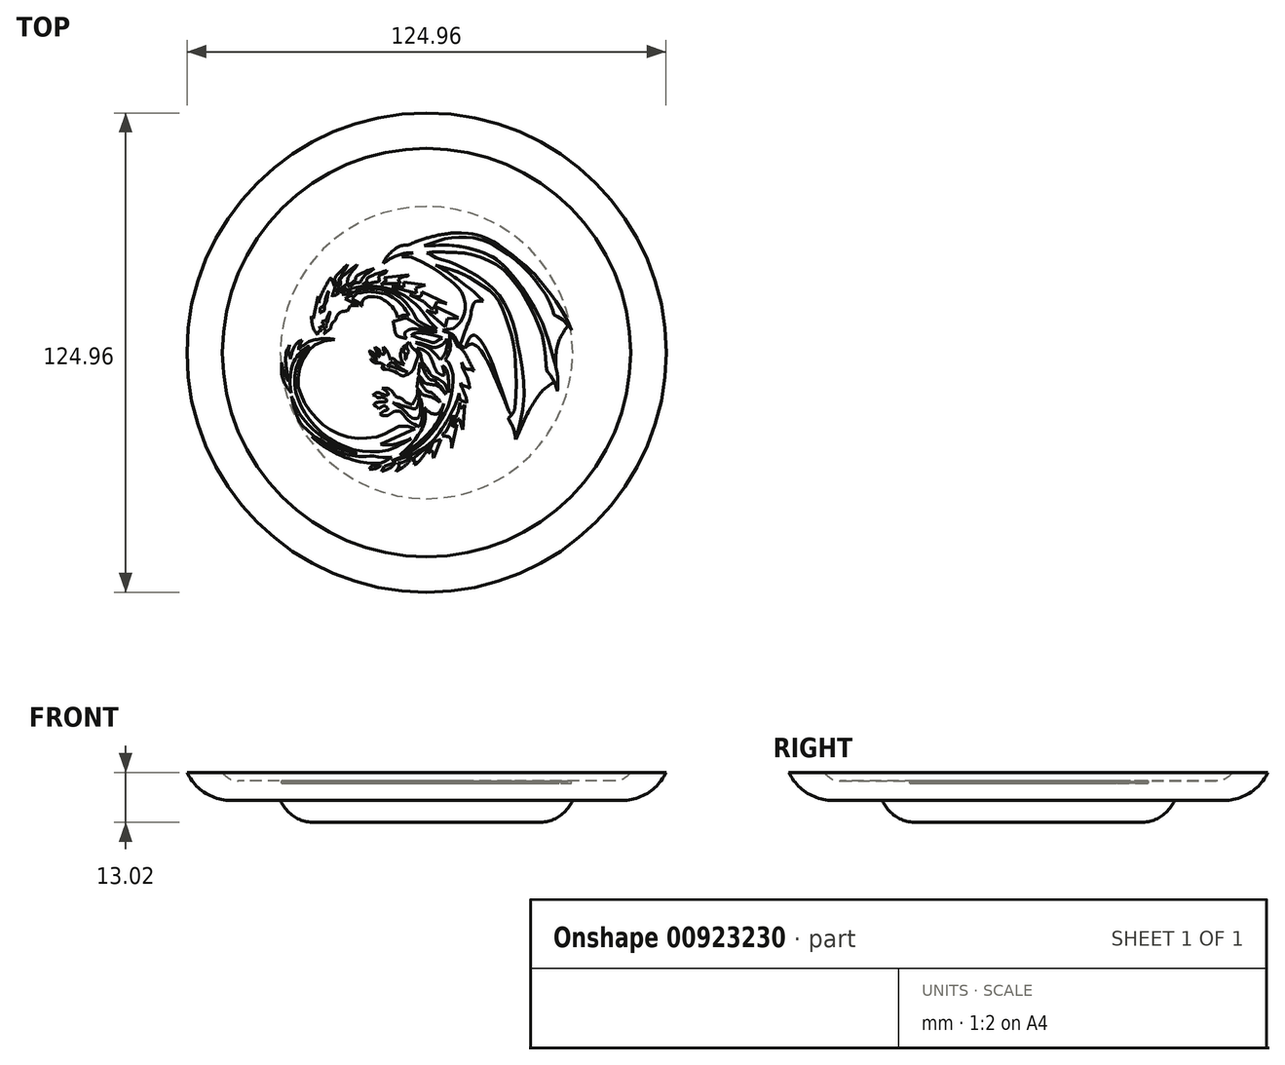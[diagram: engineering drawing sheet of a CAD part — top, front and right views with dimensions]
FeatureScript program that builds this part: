
annotation { "Feature Type Name" : "Feature", "Feature Type Description" : "" }
export const myFeature = defineFeature(function(context is Context, id is Id, definition is map)
    precondition{}
    {
        {
            var Q0;
            Q0=qCreatedBy(makeId("Top.planeOp"),FACE);
            var sketch = newSketch(context, id + "F0", { "sketchPlane" : qUnion([Q0])});
            skCircle(sketch, "E0", {"center": v(0, 0) * mm, "radius": 62.48 * mm});
            skSolve(sketch);
        }
        {
            var Q0;
            Q0=makeQuery(id+"F0.imprint","IMPRINT",FACE,{"disambiguationData":[TD([[makeQuery(id+"F0.imprint","IMPRINT",EDGE,{"derivedFrom":sQuery(id+"F0.wireOp",EDGE,"E0")}),1.0]])]});
            extrude(context, id + "F1", {"entities" : qUnion([Q0]), "depth" : 5.08 * mm, "offsetDistance" : 25.4 * mm});
        }
        {
            var Q0;
            Q0=makeQuery(id+"F1.opExtrude","CAP_FACE",FACE,{"disambiguationData":[OSD([sQuery(id+"F0.wireOp",EDGE,"E0")])],"isStart":false});
            var sketch = newSketch(context, id + "F2", { "sketchPlane" : qUnion([Q0])});
            skCircle(sketch, "E1", {"center": v(0, 0) * mm, "radius": 62.48 * mm});
            skCircle(sketch, "E2", {"center": v(0, 0) * mm, "radius": 53.23 * mm});
            skSolve(sketch);
        }
        {
            var Q0;
            Q0 = qSketchRegion(id + "F2", true);
            extrude(context, id + "F3", {"entities" : qUnion([Q0]), "endBound" : BoundingType.SYMMETRIC, "depth" : 4.44 * mm, "offsetDistance" : 25.4 * mm});
        }
        {
            var Q0;
            Q0=makeQuery(id+"F1.opExtrude","SWEPT_BODY",BODY,{"disambiguationData":[OSD([sQuery(id+"F0.wireOp",EDGE,"E0")])]});
            var Q1;
            Q1=makeQuery(id+"F3.opExtrude","SWEPT_BODY",BODY,{"disambiguationData":[OSD([sQuery(id+"F2.wireOp",EDGE,"E1"),sQuery(id+"F2.wireOp",EDGE,"E2")])]});
            booleanBodies(context, id + "F4", {"operationType" : BooleanOperationType.UNION, "tools" : qUnion([Q0, Q1])});
        }
        {
            var Q0;
            Q0=makeQuery(id+"F1.opExtrude","CAP_FACE",FACE,{"disambiguationData":[OSD([sQuery(id+"F0.wireOp",EDGE,"E0")])],"isStart":false});
            fillet(context, id + "F5", {"entities" : qUnion([Q0]), "radius" : 5.08 * mm, "tangentPropagation" : true, "allowEdgeOverflow" : false});
        }
        {
            var Q0;
            Q0=makeQuery(id+"F1.opExtrude","CAP_FACE",FACE,{"disambiguationData":[OSD([sQuery(id+"F0.wireOp",EDGE,"E0")])],"isStart":true});
            var sketch = newSketch(context, id + "F6", { "sketchPlane" : qUnion([Q0])});
            skCircle(sketch, "E3", {"center": v(0, 0) * mm, "radius": 38.1 * mm});
            skSolve(sketch);
        }
        {
            var Q0;
            Q0 = qSketchRegion(id + "F6", true);
            extrude(context, id + "F7", {"entities" : qUnion([Q0]), "operationType" : NewBodyOperationType.ADD, "depth" : 5.7 * mm, "offsetDistance" : 25.4 * mm});
        }
        {
            var Q0;
            Q0=makeQuery(id+"F7.opExtrude","CAP_EDGE",EDGE,{"disambiguationData":[OSD([sQuery(id+"F6.wireOp",EDGE,"E3")])],"isStart":false});
            fillet(context, id + "F8", {"entities" : qUnion([Q0]), "radius" : 9.52 * mm, "tangentPropagation" : true, "allowEdgeOverflow" : false});
        }
        {
            var Q0;
            Q0=makeQuery(id+"F1.opExtrude","CAP_EDGE",EDGE,{"disambiguationData":[OSD([sQuery(id+"F0.wireOp",EDGE,"E0")])],"isStart":true});
            fillet(context, id + "F9", {"entities" : qUnion([Q0]), "radius" : 12.7 * mm, "tangentPropagation" : true, "allowEdgeOverflow" : false});
        }
        {
            var Q0;
            Q0=makeQuery(id+"F1.opExtrude","CAP_FACE",FACE,{"disambiguationData":[OSD([sQuery(id+"F0.wireOp",EDGE,"E0")])],"isStart":false});
            var sketch = newSketch(context, id + "F10", { "sketchPlane" : qUnion([Q0])});
            skFitSpline(sketch, "E4", {"points": [v(-28.04, 12.93) * mm, v(-27.98, 13.48) * mm, v(-27.55, 14.77) * mm, v(-26.14, 17.67) * mm, v(-25, 19.57) * mm], "startDerivative": vector(0.19, 3.57) * mm, "endDerivative": vector(3.86, 6) * mm});
            skFitSpline(sketch, "E5", {"points": [v(-25, 19.57) * mm, v(-24.5, 18.6) * mm, v(-24.1, 17.53) * mm, v(-23.93, 16.84) * mm, v(-24.33, 15.58) * mm, v(-24.62, 14.6) * mm], "startDerivative": vector(2.5, -4.6) * mm, "endDerivative": vector(-1.17, -4.66) * mm});
            skFitSpline(sketch, "E6", {"points": [v(-24.62, 14.6) * mm, v(-24.27, 14.9) * mm, v(-23.9, 14.9) * mm, v(-23.18, 15.35) * mm, v(-20.91, 16.98) * mm], "startDerivative": vector(1.88, 2.32) * mm, "endDerivative": vector(5.97, 4.22) * mm});
            skLineSegment(sketch, "E7", {"start": v(-20.91, 16.98) * mm, "end": v(-22.03, 15.17) * mm});
            skLineSegment(sketch, "E8", {"start": v(-22.03, 15.17) * mm, "end": v(-19.25, 15.17) * mm});
            skLineSegment(sketch, "E9", {"start": v(-19.25, 15.17) * mm, "end": v(-21.26, 14) * mm});
            skLineSegment(sketch, "E10", {"start": v(-21.26, 14) * mm, "end": v(-17.72, 12.3) * mm});
            skLineSegment(sketch, "E11", {"start": v(-17.72, 12.3) * mm, "end": v(-19.9, 12.3) * mm});
            skLineSegment(sketch, "E12", {"start": v(-19.9, 12.3) * mm, "end": v(-20.63, 10.8) * mm});
            skFitSpline(sketch, "E13", {"points": [v(-23.96, 8.22) * mm, v(-23.64, 8.88) * mm, v(-23.27, 9.66) * mm, v(-22.87, 10.17) * mm, v(-22.3, 10.55) * mm, v(-21.57, 10.78) * mm, v(-20.63, 10.8) * mm], "startDerivative": vector(1.92, 3.92) * mm, "endDerivative": vector(5.3, -0.13) * mm});
            skFitSpline(sketch, "E14", {"points": [v(-23.96, 8.22) * mm, v(-24.48, 7.82) * mm, v(-24.8, 7.27) * mm, v(-25, 6.3) * mm], "startDerivative": vector(-1.8, -1.2) * mm, "endDerivative": vector(-0.42, -2.73) * mm});
            skFitSpline(sketch, "E15", {"points": [v(-25, 6.3) * mm, v(-26.69, 4.89) * mm], "startDerivative": vector(-1.7, -1.4) * mm, "endDerivative": vector(-1.7, -1.4) * mm});
            skFitSpline(sketch, "E16", {"points": [v(-26.69, 4.89) * mm, v(-26.49, 5.38) * mm, v(-26.39, 5.7) * mm, v(-26.47, 5.99) * mm, v(-26.93, 6.3) * mm], "startDerivative": vector(0.76, 1.83) * mm, "endDerivative": vector(-1.93, 0.98) * mm});
            skFitSpline(sketch, "E17", {"points": [v(-26.93, 6.3) * mm, v(-26.45, 6.45) * mm, v(-26.1, 6.7) * mm, v(-26.06, 7.11) * mm, v(-26.27, 7.38) * mm], "startDerivative": vector(1.79, 0.52) * mm, "endDerivative": vector(-1.18, 1.01) * mm});
            skFitSpline(sketch, "E18", {"points": [v(-26.27, 7.38) * mm, v(-25.96, 7.8) * mm, v(-25.68, 8.47) * mm, v(-25.53, 8.96) * mm, v(-25.34, 9.66) * mm, v(-25.25, 10.1) * mm, v(-25.2, 10.57) * mm, v(-25.4, 10.34) * mm, v(-25.7, 9.62) * mm, v(-25.98, 8.75) * mm, v(-25.98, 8.6) * mm], "startDerivative": vector(3.31, 3.75) * mm, "endDerivative": vector(0.36, -2.21) * mm});
            skFitSpline(sketch, "E19", {"points": [v(-25.98, 8.6) * mm, v(-26.66, 8.26) * mm, v(-27.38, 8.02) * mm], "startDerivative": vector(-1.34, -0.73) * mm, "endDerivative": vector(-1.45, -0.45) * mm});
            skFitSpline(sketch, "E20", {"points": [v(-27.87, 6.76) * mm, v(-27.52, 6.73) * mm, v(-27.17, 6.84) * mm, v(-26.63, 7.18) * mm], "startDerivative": vector(1.2, -0.18) * mm, "endDerivative": vector(1.42, 0.96) * mm});
            skFitSpline(sketch, "E21", {"points": [v(-27.38, 8.02) * mm, v(-26.63, 7.18) * mm], "startDerivative": vector(0.75, -0.84) * mm, "endDerivative": vector(0.75, -0.84) * mm});
            skFitSpline(sketch, "E22", {"points": [v(-27.87, 6.76) * mm, v(-27.82, 6.47) * mm, v(-27.6, 6.07) * mm, v(-27.24, 5.75) * mm], "startDerivative": vector(0.1, -0.97) * mm, "endDerivative": vector(1.1, -0.77) * mm});
            skFitSpline(sketch, "E23", {"points": [v(-28.4, 4.67) * mm, v(-28.34, 4.98) * mm, v(-28.26, 5.28) * mm, v(-28, 5.63) * mm, v(-27.46, 5.74) * mm, v(-27.24, 5.75) * mm], "startDerivative": vector(0.2, 1.61) * mm, "endDerivative": vector(1.17, 0.05) * mm});
            skFitSpline(sketch, "E24", {"points": [v(-28.4, 4.67) * mm, v(-28.6, 4.85) * mm, v(-28.86, 5.17) * mm, v(-29.12, 5.54) * mm, v(-29.4, 6.03) * mm, v(-29.58, 6.52) * mm, v(-29.7, 6.9) * mm, v(-29.8, 7.36) * mm, v(-29.89, 7.96) * mm, v(-29.96, 8.44) * mm, v(-30.02, 9.03) * mm, v(-30.1, 9.47) * mm], "startDerivative": vector(-2.77, 2.4) * mm, "endDerivative": vector(-0.92, 4.7) * mm});
            skLineSegment(sketch, "E25", {"start": v(-30.1, 9.47) * mm, "end": v(-29.5, 8.8) * mm});
            skLineSegment(sketch, "E26", {"start": v(-29.5, 8.8) * mm, "end": v(-28.25, 14.66) * mm});
            skLineSegment(sketch, "E27", {"start": v(-28.25, 14.66) * mm, "end": v(-28.04, 12.93) * mm});
            skFitSpline(sketch, "E28", {"points": [v(-27.7, 11.73) * mm, v(-27.7, 10.38) * mm], "startDerivative": vector(0.01, -1.36) * mm, "endDerivative": vector(0.01, -1.36) * mm});
            skFitSpline(sketch, "E29", {"points": [v(-27.7, 11.73) * mm, v(-27.38, 11.83) * mm, v(-27.1, 12.04) * mm, v(-26.88, 12.27) * mm, v(-26.57, 13) * mm, v(-25.8, 15.63) * mm, v(-25.7, 15.87) * mm, v(-25.64, 15.94) * mm, v(-25.62, 15.76) * mm, v(-26.3, 12.85) * mm, v(-26.63, 12.03) * mm, v(-26.64, 11.17) * mm], "startDerivative": vector(5.23, 1.12) * mm, "endDerivative": vector(0.62, -9.26) * mm});
            skFitSpline(sketch, "E30", {"points": [v(-27.7, 10.38) * mm, v(-27.52, 10.55) * mm, v(-27.27, 10.67) * mm, v(-26.95, 10.73) * mm, v(-26.75, 10.88) * mm, v(-26.64, 11.17) * mm], "startDerivative": vector(0.88, 1.01) * mm, "endDerivative": vector(0.41, 1.5) * mm});
            skFitSpline(sketch, "E31", {"points": [v(-8.75, 8.21) * mm, v(-8.37, 8.23) * mm, v(-7.9, 8.3) * mm, v(-7.35, 8.47) * mm, v(-6.92, 8.66) * mm, v(-6.56, 8.77) * mm, v(-6.14, 8.89) * mm, v(-5.65, 8.94) * mm, v(-5.17, 8.94) * mm, v(-4.69, 8.76) * mm, v(-4.16, 8.44) * mm, v(-3.7, 8.16) * mm, v(-3.22, 7.83) * mm, v(-2.67, 7.43) * mm, v(-2.24, 7.19) * mm, v(-1.71, 6.89) * mm, v(-1.07, 6.57) * mm, v(-0.5, 6.34) * mm, v(0, 6.16) * mm, v(0.75, 5.96) * mm, v(1.44, 5.83) * mm, v(1.97, 5.78) * mm], "startDerivative": vector(9.36, 0.14) * mm, "endDerivative": vector(10.96, -0.78) * mm});
            skFitSpline(sketch, "E32", {"points": [v(-8.75, 8.21) * mm, v(-8.66, 7.74) * mm, v(-8.54, 7.27) * mm, v(-8.4, 6.67) * mm, v(-8.3, 6.08) * mm, v(-8.21, 5.56) * mm, v(-8.12, 5.16) * mm, v(-8, 4.8) * mm, v(-7.8, 4.5) * mm, v(-7.48, 4.27) * mm, v(-7.03, 4.09) * mm, v(-6.6, 3.96) * mm, v(-6.25, 3.87) * mm, v(-5.75, 3.75) * mm, v(-5.15, 3.68) * mm], "startDerivative": vector(1.31, -6.58) * mm, "endDerivative": vector(7.6, -0.57) * mm});
            skFitSpline(sketch, "E33", {"points": [v(1.97, 5.78) * mm, v(2.69, 5.41) * mm], "startDerivative": vector(0.71, -0.37) * mm, "endDerivative": vector(0.71, -0.37) * mm});
            skFitSpline(sketch, "E34", {"points": [v(2.69, 5.41) * mm, v(2.12, 5.41) * mm, v(1.67, 5.41) * mm, v(0.66, 5.52) * mm, v(0, 5.6) * mm, v(-0.74, 5.78) * mm, v(-1.43, 5.92) * mm, v(-2.13, 6.07) * mm, v(-2.9, 6.16) * mm, v(-3.84, 6.16) * mm, v(-4.63, 5.95) * mm, v(-5.22, 5.62) * mm, v(-5.56, 5.25) * mm, v(-5.7, 4.77) * mm, v(-5.55, 4.24) * mm, v(-5.15, 3.68) * mm], "startDerivative": vector(-9.85, 0.1) * mm, "endDerivative": vector(6.65, -8.24) * mm});
            skFitSpline(sketch, "E35", {"points": [v(-16.78, 12.16) * mm, v(-16.82, 12.74) * mm, v(-16.7, 13.46) * mm, v(-16.13, 14.1) * mm, v(-15.32, 14.47) * mm, v(-14.33, 14.58) * mm, v(-12.82, 14.44) * mm, v(-11.38, 13.89) * mm, v(-10.26, 13.15) * mm, v(-8.8, 11.77) * mm, v(-7.83, 10.11) * mm, v(-7.52, 9.13) * mm], "startDerivative": vector(-0.9, 8.75) * mm, "endDerivative": vector(2.8, -10.83) * mm});
            skFitSpline(sketch, "E36", {"points": [v(-16.78, 12.16) * mm, v(-17.1, 12.3) * mm, v(-17.33, 12.69) * mm, v(-17.6, 12.98) * mm, v(-18.03, 13.27) * mm, v(-18.72, 13.59) * mm, v(-19.13, 13.85) * mm, v(-19.36, 14.17) * mm], "startDerivative": vector(-2.84, 0.74) * mm, "endDerivative": vector(-1.6, 2.6) * mm});
            skFitSpline(sketch, "E37", {"points": [v(-19.36, 14.17) * mm, v(-18, 15.55) * mm], "startDerivative": vector(1.37, 1.38) * mm, "endDerivative": vector(1.37, 1.38) * mm});
            skFitSpline(sketch, "E38", {"points": [v(-18, 15.55) * mm, v(-17.5, 15.55) * mm, v(-16.78, 15.7) * mm, v(-16.13, 15.8) * mm, v(-15.35, 15.89) * mm, v(-14.44, 15.87) * mm, v(-13.17, 15.77) * mm, v(-11.9, 15.55) * mm, v(-10.25, 15.09) * mm, v(-8.98, 14.47) * mm, v(-7.38, 13.33) * mm, v(-6.44, 12.45) * mm, v(-5.38, 11.06) * mm, v(-4.59, 9.63) * mm], "startDerivative": vector(9.45, -0.58) * mm, "endDerivative": vector(8.06, -15.64) * mm});
            skFitSpline(sketch, "E39", {"points": [v(-7.52, 9.13) * mm, v(-7.08, 9.34) * mm, v(-6.6, 9.58) * mm, v(-5.82, 9.75) * mm, v(-4.59, 9.63) * mm], "startDerivative": vector(2.07, 1.08) * mm, "endDerivative": vector(4.13, -0.76) * mm});
            skFitSpline(sketch, "E40", {"points": [v(-20.93, 15.76) * mm, v(-20.63, 16.11) * mm, v(-19.99, 16.5) * mm, v(-19.04, 16.83) * mm, v(-17.63, 17.11) * mm, v(-15.8, 17.3) * mm, v(-13.72, 17.3) * mm, v(-12.44, 17.16) * mm, v(-11.33, 17) * mm, v(-9.91, 16.68) * mm, v(-8.5, 16.23) * mm, v(-7, 15.55) * mm, v(-5.54, 14.68) * mm, v(-4.57, 14.02) * mm, v(-3.54, 13.25) * mm, v(-2.5, 12.23) * mm, v(-1.52, 11.2) * mm, v(-0.68, 10.23) * mm, v(0.3, 8.93) * mm, v(0.9, 8.06) * mm, v(2.29, 6.68) * mm, v(2.77, 6.22) * mm], "startDerivative": vector(9.28, 12.83) * mm, "endDerivative": vector(11.69, -11.13) * mm});
            skFitSpline(sketch, "E41", {"points": [v(2.77, 6.22) * mm, v(1.24, 6.52) * mm, v(-0.86, 7.43) * mm, v(-2.01, 8.21) * mm, v(-2.67, 8.79) * mm, v(-3.1, 9.68) * mm, v(-3.67, 10.76) * mm, v(-4.37, 11.75) * mm, v(-5.48, 13.1) * mm, v(-6.98, 14.44) * mm, v(-8.75, 15.45) * mm, v(-11.33, 16.33) * mm, v(-13.54, 16.68) * mm, v(-15.96, 16.68) * mm, v(-18.37, 16.08) * mm, v(-18.84, 15.66) * mm], "startDerivative": vector(-22.2, 3.08) * mm, "endDerivative": vector(-1.37, -8.56) * mm});
            skFitSpline(sketch, "E42", {"points": [v(-20.93, 15.76) * mm, v(-18.84, 15.66) * mm], "startDerivative": vector(2.1, -0.1) * mm, "endDerivative": vector(2.1, -0.1) * mm});
            skFitSpline(sketch, "E43", {"points": [v(-3.95, 4.44) * mm, v(-3.72, 4.65) * mm, v(-3.26, 4.95) * mm, v(-2.39, 5.16) * mm, v(-1.16, 5.08) * mm, v(2.74, 4.34) * mm, v(4.1, 3.8) * mm], "startDerivative": vector(2.53, 2.3) * mm, "endDerivative": vector(5.84, -2.9) * mm});
            skFitSpline(sketch, "E44", {"points": [v(4.1, 3.8) * mm, v(3.23, 3.31) * mm, v(2.56, 2.8) * mm, v(1.94, 2.6) * mm, v(0.3, 2.95) * mm, v(-3.95, 4.44) * mm], "startDerivative": vector(-5.6, -2.77) * mm, "endDerivative": vector(-13.5, 4.87) * mm});
            skFitSpline(sketch, "E45", {"points": [v(5.26, 3.68) * mm, v(5.33, 3) * mm, v(5.38, 2.06) * mm, v(5.16, 0.74) * mm, v(4.49, -0.78) * mm, v(4.04, -1.43) * mm, v(3.64, -1.88) * mm], "startDerivative": vector(0.54, -4.67) * mm, "endDerivative": vector(-2.9, -3.43) * mm});
            skFitSpline(sketch, "E46", {"points": [v(-2.87, 2.6) * mm, v(-1.8, 2.5) * mm, v(-0.65, 2.16) * mm, v(0.37, 1.73) * mm, v(1.37, 1.46) * mm, v(2.44, 1.39) * mm, v(3.71, 1.8) * mm, v(4.69, 2.6) * mm, v(5.26, 3.68) * mm], "startDerivative": vector(8.83, -0.4) * mm, "endDerivative": vector(3.84, 8.84) * mm});
            skFitSpline(sketch, "E47", {"points": [v(-2.5, 1.28) * mm, v(-1.2, 0.82) * mm, v(0.33, -0.2) * mm, v(1.03, -1.2) * mm, v(1.67, -2.59) * mm, v(2.37, -4.54) * mm, v(3.36, -5.62) * mm, v(4.44, -5.9) * mm, v(4.79, -5.67) * mm], "startDerivative": vector(9.7, -2.95) * mm, "endDerivative": vector(4, 4.29) * mm});
            skFitSpline(sketch, "E48", {"points": [v(-2.87, 2.6) * mm, v(-1.76, 2.16) * mm, v(-0.48, 1.7) * mm, v(0.83, 1.02) * mm, v(1.93, 0) * mm, v(3.64, -1.88) * mm], "startDerivative": vector(6.15, -2.7) * mm, "endDerivative": vector(6.76, -8.1) * mm});
            skFitSpline(sketch, "E49", {"points": [v(4.79, -5.67) * mm, v(4.1, -3.41) * mm], "startDerivative": vector(-0.7, 2.26) * mm, "endDerivative": vector(-0.7, 2.26) * mm});
            skFitSpline(sketch, "E50", {"points": [v(5.77, -10.5) * mm, v(5.32, -9.46) * mm, v(5.04, -8.67) * mm, v(4.75, -8.15) * mm, v(4.18, -7.63) * mm, v(2.9, -6.85) * mm, v(1.65, -6.18) * mm, v(1.13, -5.73) * mm, v(0.44, -4.71) * mm, v(0, -3.9) * mm, v(-0.53, -3.15) * mm, v(-1.03, -2.58) * mm, v(-1.27, -1.9) * mm, v(-1.46, -0.82) * mm, v(-1.58, -0.3) * mm, v(-2, 0.48) * mm, v(-2.5, 1.28) * mm], "startDerivative": vector(-6.97, 15.32) * mm, "endDerivative": vector(-7.53, 12.46) * mm});
            skFitSpline(sketch, "E51", {"points": [v(4.1, -3.41) * mm, v(4.59, -3.67) * mm, v(5.13, -4.31) * mm, v(5.49, -5.21) * mm, v(5.68, -6.52) * mm, v(5.77, -10.5) * mm], "startDerivative": vector(3.88, -1.58) * mm, "endDerivative": vector(0.12, -13.13) * mm});
            skFitSpline(sketch, "E52", {"points": [v(-1.67, -2.53) * mm, v(-2.05, -5.8) * mm], "startDerivative": vector(-0.39, -3.27) * mm, "endDerivative": vector(-0.39, -3.27) * mm});
            skFitSpline(sketch, "E53", {"points": [v(-1.67, -2.53) * mm, v(-0.96, -4.03) * mm, v(-0.37, -5.41) * mm, v(0.33, -6.48) * mm, v(1.15, -7.1) * mm, v(1.94, -7.25) * mm, v(2.78, -7.89) * mm, v(3.8, -8.91) * mm, v(4.96, -10.5) * mm], "startDerivative": vector(5.26, -10.7) * mm, "endDerivative": vector(7.48, -11.1) * mm});
            skFitSpline(sketch, "E54", {"points": [v(4.96, -10.5) * mm, v(4.96, -10.86) * mm], "startDerivative": vector(0, -0.36) * mm, "endDerivative": vector(0, -0.36) * mm});
            skFitSpline(sketch, "E55", {"points": [v(4.96, -10.86) * mm, v(4.7, -10.5) * mm, v(4.1, -9.73) * mm, v(3.41, -9.04) * mm, v(2.47, -8.54) * mm, v(1.1, -8.31) * mm, v(0.2, -8.16) * mm, v(-0.46, -7.85) * mm, v(-1.27, -6.8) * mm, v(-2.05, -5.8) * mm], "startDerivative": vector(-3.06, 4.38) * mm, "endDerivative": vector(-6.25, 7.43) * mm});
            skFitSpline(sketch, "E56", {"points": [v(-2.12, -6.24) * mm, v(-2.48, -9.1) * mm], "startDerivative": vector(-0.28, -2.87) * mm, "endDerivative": vector(-0.28, -2.87) * mm});
            skFitSpline(sketch, "E57", {"points": [v(3.5, -12.63) * mm, v(3.5, -13) * mm], "startDerivative": vector(-0.02, -0.37) * mm, "endDerivative": vector(-0.02, -0.37) * mm});
            skFitSpline(sketch, "E58", {"points": [v(-2.48, -9.1) * mm, v(-1.34, -10.62) * mm, v(-1, -10.96) * mm, v(0, -11.29) * mm, v(1.64, -11.76) * mm, v(3.16, -12.67) * mm, v(3.5, -13) * mm], "startDerivative": vector(5.4, -8.78) * mm, "endDerivative": vector(2.33, -2.73) * mm});
            skFitSpline(sketch, "E59", {"points": [v(-2.12, -6.24) * mm, v(-1.33, -8.01) * mm, v(-0.96, -8.78) * mm, v(-0.5, -9.5) * mm, v(0, -10.04) * mm, v(0.7, -10.29) * mm, v(1.42, -10.56) * mm, v(2.38, -11.43) * mm, v(3.5, -12.63) * mm], "startDerivative": vector(5.15, -11.65) * mm, "endDerivative": vector(7.3, -7.88) * mm});
            skFitSpline(sketch, "E60", {"points": [v(-0.54, -14.34) * mm, v(0, -14.94) * mm, v(0.7, -15.52) * mm, v(1.85, -16.02) * mm, v(2.86, -15.87) * mm, v(3.82, -14.87) * mm, v(4.47, -13.3) * mm], "startDerivative": vector(3.55, -4.47) * mm, "endDerivative": vector(2.7, 8.16) * mm});
            skFitSpline(sketch, "E61", {"points": [v(-6.96, -26.68) * mm, v(-5.37, -25.78) * mm, v(-2.57, -23.93) * mm, v(0, -21.6) * mm, v(1.91, -19.35) * mm, v(3.5, -16.56) * mm, v(4.47, -13.3) * mm], "startDerivative": vector(11.38, 6.23) * mm, "endDerivative": vector(4.5, 18.8) * mm});
            skFitSpline(sketch, "E62", {"points": [v(-0.54, -14.34) * mm, v(-0.28, -15.56) * mm, v(-0.28, -16.48) * mm, v(-0.54, -18.3) * mm, v(-1.8, -20.95) * mm, v(-3.86, -23.76) * mm, v(-6.96, -26.68) * mm], "startDerivative": vector(2.65, -10.49) * mm, "endDerivative": vector(-14.5, -12.62) * mm});
            skFitSpline(sketch, "E63", {"points": [v(-4.47, 2.76) * mm, v(-5.14, 2.27) * mm], "startDerivative": vector(-0.67, -0.49) * mm, "endDerivative": vector(-0.67, -0.49) * mm});
            skFitSpline(sketch, "E64", {"points": [v(-4.47, 2.76) * mm, v(-4.27, 2.17) * mm, v(-3.7, 1.27) * mm, v(-2.88, 0.52) * mm, v(-2.37, 0) * mm, v(-2.17, -0.5) * mm, v(-2.31, -1.4) * mm, v(-2.92, -3.08) * mm, v(-3.64, -4.8) * mm, v(-4.47, -5.5) * mm, v(-5.37, -5.9) * mm, v(-5.94, -6.07) * mm, v(-6.47, -6.05) * mm, v(-7.34, -5.52) * mm, v(-8.03, -5.08) * mm, v(-8.85, -4.71) * mm, v(-9.8, -4.43) * mm, v(-10.68, -4.36) * mm, v(-11.31, -4.36) * mm, v(-11.54, -4.18) * mm, v(-11.7, -3.9) * mm, v(-11.45, -3.63) * mm, v(-10.9, -3.45) * mm], "startDerivative": vector(3.99, -13.9) * mm, "endDerivative": vector(14.88, 3.67) * mm});
            skFitSpline(sketch, "E65", {"points": [v(-5.14, 2.27) * mm, v(-5.14, 1.91) * mm, v(-5.14, 1.14) * mm, v(-4.73, 0.35) * mm, v(-4.75, 0) * mm, v(-5.04, -0.44) * mm, v(-5.39, -1.8) * mm], "startDerivative": vector(0.18, -3.36) * mm, "endDerivative": vector(-1.16, -6.53) * mm});
            skFitSpline(sketch, "E66", {"points": [v(-5.39, -1.8) * mm, v(-5.54, -1.8) * mm, v(-5.57, -1.32) * mm, v(-5.54, -0.37) * mm, v(-5.71, -0.11) * mm, v(-5.93, 0.16) * mm, v(-5.96, 0.58) * mm, v(-5.56, 1.9) * mm], "startDerivative": vector(-2.31, -0.59) * mm, "endDerivative": vector(2.23, 6.4) * mm});
            skFitSpline(sketch, "E67", {"points": [v(-5.56, 1.9) * mm, v(-5.97, 1.54) * mm, v(-6.65, 0.25) * mm, v(-6.78, -0.89) * mm, v(-6.53, -1.92) * mm, v(-5.79, -3.15) * mm], "startDerivative": vector(-2.8, -1.88) * mm, "endDerivative": vector(3.87, -5.33) * mm});
            skFitSpline(sketch, "E68", {"points": [v(-9.4, -1.99) * mm, v(-9.27, -1.76) * mm, v(-9.04, -1.54) * mm, v(-8.65, -1.62) * mm, v(-8.25, -1.95) * mm, v(-7.5, -2.5) * mm, v(-6.9, -2.84) * mm, v(-6.07, -3.1) * mm, v(-5.79, -3.15) * mm], "startDerivative": vector(1.29, 2.48) * mm, "endDerivative": vector(2.56, -0.43) * mm});
            skFitSpline(sketch, "E69", {"points": [v(-11.26, 1.44) * mm, v(-10.42, 0.54) * mm, v(-9.92, -0.37) * mm, v(-9.4, -1.99) * mm], "startDerivative": vector(2.85, -2.75) * mm, "endDerivative": vector(1.34, -4.6) * mm});
            skFitSpline(sketch, "E70", {"points": [v(-11.26, 1.44) * mm, v(-11.26, 0.61) * mm, v(-10.99, 0) * mm, v(-10.99, -0.4) * mm, v(-11.26, -0.46) * mm, v(-11.75, -0.34) * mm, v(-12.12, 0) * mm, v(-12.26, 0.66) * mm], "startDerivative": vector(-0.57, -4.87) * mm, "endDerivative": vector(0.04, 4.39) * mm});
            skFitSpline(sketch, "E71", {"points": [v(-12.26, 0.66) * mm, v(-13.35, 1.47) * mm], "startDerivative": vector(-1.1, 0.8) * mm, "endDerivative": vector(-1.1, 0.8) * mm});
            skFitSpline(sketch, "E72", {"points": [v(-13.35, 1.47) * mm, v(-13.35, 0.99) * mm, v(-13.2, 0.45) * mm, v(-12.75, -0.32) * mm, v(-12.4, -0.69) * mm, v(-12.26, -0.94) * mm, v(-12.46, -1.12) * mm, v(-12.8, -1.1) * mm, v(-13.23, -0.77) * mm, v(-13.7, -0.2) * mm, v(-13.88, 0) * mm], "startDerivative": vector(-0.26, -4.77) * mm, "endDerivative": vector(-1.9, 2.34) * mm});
            skFitSpline(sketch, "E73", {"points": [v(-14.79, 0.56) * mm, v(-14.47, 0.26) * mm, v(-14.24, 0.1) * mm, v(-13.88, 0) * mm], "startDerivative": vector(0.89, -0.88) * mm, "endDerivative": vector(1.14, -0.2) * mm});
            skFitSpline(sketch, "E74", {"points": [v(-14.79, 0.56) * mm, v(-14.79, 0.16) * mm, v(-14.57, -0.42) * mm, v(-13.75, -1.13) * mm, v(-13.22, -1.47) * mm, v(-12.99, -1.8) * mm, v(-12.95, -2) * mm, v(-13.26, -2.08) * mm, v(-13.94, -1.92) * mm, v(-14.56, -1.66) * mm], "startDerivative": vector(-0.24, -4.02) * mm, "endDerivative": vector(-4.83, 2.1) * mm});
            skFitSpline(sketch, "E75", {"points": [v(-14.56, -1.66) * mm, v(-14.36, -2.04) * mm, v(-13.83, -2.5) * mm, v(-13.35, -2.72) * mm, v(-12.66, -2.72) * mm, v(-12.12, -2.72) * mm, v(-11.56, -2.96) * mm, v(-11.13, -3.27) * mm, v(-10.9, -3.45) * mm], "startDerivative": vector(1.32, -3.34) * mm, "endDerivative": vector(2.27, -1.83) * mm});
            skFitSpline(sketch, "E76", {"points": [v(-9.13, -2.6) * mm, v(-8.81, -2.6) * mm, v(-8.3, -2.94) * mm, v(-7.34, -3.62) * mm, v(-5.7, -4.76) * mm, v(-4.95, -5.12) * mm], "startDerivative": vector(2.63, 0.3) * mm, "endDerivative": vector(3.48, -1.42) * mm});
            skFitSpline(sketch, "E77", {"points": [v(-10.4, -3.47) * mm, v(-9.94, -3.22) * mm, v(-9.42, -2.7) * mm, v(-9.13, -2.6) * mm], "startDerivative": vector(1.33, 0.53) * mm, "endDerivative": vector(1.04, 0.24) * mm});
            skFitSpline(sketch, "E78", {"points": [v(-10.4, -3.47) * mm, v(-8.9, -3.71) * mm, v(-6.79, -4.47) * mm, v(-4.95, -5.12) * mm], "startDerivative": vector(4.78, -0.5) * mm, "endDerivative": vector(5.27, -1.78) * mm});
            skFitSpline(sketch, "E79", {"points": [v(-2.36, -9.73) * mm, v(-2.32, -10.62) * mm, v(-2.51, -11.42) * mm, v(-3.24, -12.76) * mm, v(-3.71, -13.58) * mm], "startDerivative": vector(0.34, -4.07) * mm, "endDerivative": vector(-1.8, -3.12) * mm});
            skFitSpline(sketch, "E80", {"points": [v(-3.71, -13.58) * mm, v(-5.64, -12.87) * mm], "startDerivative": vector(-1.93, 0.7) * mm, "endDerivative": vector(-1.93, 0.7) * mm});
            skFitSpline(sketch, "E81", {"points": [v(-5.64, -12.87) * mm, v(-6.08, -12.32) * mm, v(-6.42, -12.03) * mm, v(-7.1, -11.75) * mm, v(-7.63, -11.65) * mm, v(-8.16, -11.36) * mm, v(-8.6, -10.62) * mm, v(-9.82, -9.51) * mm, v(-11.56, -9.26) * mm], "startDerivative": vector(-4.07, 5.36) * mm, "endDerivative": vector(-10.12, 0) * mm});
            skFitSpline(sketch, "E82", {"points": [v(-11.56, -9.26) * mm, v(-10.64, -9.95) * mm, v(-10.02, -10.62) * mm, v(-10, -10.96) * mm, v(-10.4, -11.15) * mm, v(-11.1, -11) * mm, v(-11.94, -10.62) * mm, v(-12.8, -10.41) * mm, v(-13.98, -11.07) * mm], "startDerivative": vector(6.26, -4.35) * mm, "endDerivative": vector(-7.5, -5.67) * mm});
            skFitSpline(sketch, "E83", {"points": [v(-13.98, -11.07) * mm, v(-13.24, -11.33) * mm, v(-12.78, -11.85) * mm], "startDerivative": vector(1.56, -0.34) * mm, "endDerivative": vector(0.84, -1.22) * mm});
            skFitSpline(sketch, "E84", {"points": [v(-12.78, -11.85) * mm, v(-12.12, -11.67) * mm, v(-10.9, -11.85) * mm, v(-10.4, -12.35) * mm, v(-10.68, -12.87) * mm, v(-12.12, -12.87) * mm, v(-13.23, -13.17) * mm, v(-13.83, -13.75) * mm], "startDerivative": vector(4.76, 1.83) * mm, "endDerivative": vector(-3.96, -4.67) * mm});
            skFitSpline(sketch, "E85", {"points": [v(-13.83, -13.75) * mm, v(-13.17, -13.99) * mm, v(-12.55, -14.63) * mm], "startDerivative": vector(1.46, -0.33) * mm, "endDerivative": vector(1.1, -1.4) * mm});
            skFitSpline(sketch, "E86", {"points": [v(-12.55, -14.63) * mm, v(-11.56, -14.12) * mm, v(-10.9, -13.9) * mm, v(-10.4, -14.26) * mm, v(-10.04, -14.63) * mm], "startDerivative": vector(3.3, 1.66) * mm, "endDerivative": vector(1.57, -1.66) * mm});
            skFitSpline(sketch, "E87", {"points": [v(-10.04, -14.63) * mm, v(-10.25, -14.94) * mm, v(-11.26, -15.25) * mm], "startDerivative": vector(-0.38, -0.9) * mm, "endDerivative": vector(-1.94, -0.4) * mm});
            skFitSpline(sketch, "E88", {"points": [v(-11.26, -15.25) * mm, v(-12.12, -16.08) * mm], "startDerivative": vector(-0.86, -0.84) * mm, "endDerivative": vector(-0.86, -0.84) * mm});
            skFitSpline(sketch, "E89", {"points": [v(-12.12, -16.08) * mm, v(-11.26, -16.44) * mm, v(-10.4, -16.46) * mm, v(-9.5, -16.08) * mm, v(-8.59, -15.48) * mm, v(-7.6, -15.25) * mm, v(-6.67, -15.53) * mm, v(-5.64, -16.8) * mm, v(-4.08, -18.2) * mm, v(-1.8, -19.38) * mm], "startDerivative": vector(9, -4.54) * mm, "endDerivative": vector(15.3, -6.96) * mm});
            skFitSpline(sketch, "E90", {"points": [v(-1.55, -12.02) * mm, v(-1.34, -12.87) * mm, v(-1.15, -14.13) * mm, v(-1.06, -15.6) * mm, v(-1.08, -16.8) * mm, v(-1.8, -19.38) * mm], "startDerivative": vector(1.4, -5.21) * mm, "endDerivative": vector(-3.48, -10.46) * mm});
            skFitSpline(sketch, "E91", {"points": [v(-1.55, -12.02) * mm, v(-1.55, -13.58) * mm, v(-1.55, -14.63) * mm, v(-1.8, -16.38) * mm, v(-2.42, -17.13) * mm, v(-3.57, -17.14) * mm, v(-4.95, -16.08) * mm, v(-5.86, -15.07) * mm, v(-7, -14.22) * mm, v(-8.69, -13.15) * mm, v(-8.8, -13.05) * mm], "startDerivative": vector(-0.08, -15) * mm, "endDerivative": vector(-1.7, 2.88) * mm});
            skFitSpline(sketch, "E92", {"points": [v(-8.8, -13.05) * mm, v(-5.64, -14.03) * mm, v(-3.5, -14.63) * mm, v(-2.78, -14.63) * mm, v(-2.1, -13.05) * mm, v(-1.8, -11.07) * mm], "startDerivative": vector(12.22, -4.07) * mm, "endDerivative": vector(0.05, 9.27) * mm});
            skFitSpline(sketch, "E93", {"points": [v(-1.8, -11.07) * mm, v(-2.36, -9.73) * mm], "startDerivative": vector(-0.55, 1.34) * mm, "endDerivative": vector(-0.55, 1.34) * mm});
            skFitSpline(sketch, "E94", {"points": [v(-14.1, -29.51) * mm, v(-11.95, -29.43) * mm], "startDerivative": vector(2.16, 0.08) * mm, "endDerivative": vector(2.16, 0.08) * mm});
            skFitSpline(sketch, "E95", {"points": [v(-11.95, -29.43) * mm, v(-12.54, -29.94) * mm, v(-13.58, -30.3) * mm, v(-14.87, -30.39) * mm], "startDerivative": vector(-1.84, -1.88) * mm, "endDerivative": vector(-3.54, -0.05) * mm});
            skFitSpline(sketch, "E96", {"points": [v(-14.1, -29.51) * mm, v(-14.64, -29.9) * mm, v(-14.87, -30.39) * mm], "startDerivative": vector(-1.15, -0.67) * mm, "endDerivative": vector(-0.35, -1.08) * mm});
            skFitSpline(sketch, "E97", {"points": [v(-11.05, -29.6) * mm, v(-7.98, -28.64) * mm], "startDerivative": vector(3.06, 0.96) * mm, "endDerivative": vector(3.06, 0.96) * mm});
            skFitSpline(sketch, "E98", {"points": [v(-11.05, -29.6) * mm, v(-11.72, -30.98) * mm], "startDerivative": vector(-0.67, -1.38) * mm, "endDerivative": vector(-0.67, -1.38) * mm});
            skFitSpline(sketch, "E99", {"points": [v(-11.72, -30.98) * mm, v(-10.74, -30.7) * mm, v(-9.28, -29.94) * mm, v(-7.98, -28.64) * mm], "startDerivative": vector(3.36, 0.82) * mm, "endDerivative": vector(3.26, 3.77) * mm});
            skFitSpline(sketch, "E100", {"points": [v(-7.42, -28.81) * mm, v(-6.46, -28.7) * mm, v(-5.12, -28.1) * mm, v(-3.77, -27.12) * mm], "startDerivative": vector(3.27, 0.14) * mm, "endDerivative": vector(3.54, 2.82) * mm});
            skFitSpline(sketch, "E101", {"points": [v(-7.42, -28.81) * mm, v(-7.2, -29.6) * mm, v(-7.98, -30.98) * mm], "startDerivative": vector(0.93, -1.78) * mm, "endDerivative": vector(-1.9, -2.5) * mm});
            skFitSpline(sketch, "E102", {"points": [v(-3.77, -27.12) * mm, v(-4.41, -28.25) * mm, v(-5.57, -29.43) * mm, v(-6.8, -30.39) * mm, v(-7.98, -30.98) * mm], "startDerivative": vector(-2.36, -4.81) * mm, "endDerivative": vector(-5, -2.21) * mm});
            skFitSpline(sketch, "E103", {"points": [v(-3.84, -27.98) * mm, v(0.67, -24.2) * mm], "startDerivative": vector(4.51, 3.78) * mm, "endDerivative": vector(4.51, 3.78) * mm});
            skFitSpline(sketch, "E104", {"points": [v(0.67, -24.2) * mm, v(0.24, -25.3) * mm, v(-0.93, -27.08) * mm, v(-2.27, -28.68) * mm, v(-3.23, -29.3) * mm], "startDerivative": vector(-1.6, -4.9) * mm, "endDerivative": vector(-4.52, -2.33) * mm});
            skFitSpline(sketch, "E105", {"points": [v(-3.23, -29.3) * mm, v(-2.9, -28.07) * mm], "startDerivative": vector(0.32, 1.22) * mm, "endDerivative": vector(0.32, 1.22) * mm});
            skFitSpline(sketch, "E106", {"points": [v(-3.84, -27.98) * mm, v(-3.37, -28.17) * mm, v(-2.9, -28.07) * mm], "startDerivative": vector(0.92, -0.5) * mm, "endDerivative": vector(0.95, 0.34) * mm});
            skFitSpline(sketch, "E107", {"points": [v(1.8, -27.43) * mm, v(1.7, -27.19) * mm, v(1.69, -26.27) * mm, v(1.53, -25.75) * mm, v(1.12, -25.77) * mm, v(0.43, -26.31) * mm], "startDerivative": vector(-0.8, 1.46) * mm, "endDerivative": vector(-2.83, -2.62) * mm});
            skLineSegment(sketch, "E108", {"start": v(0.43, -26.31) * mm, "end": v(1.75, -23.3) * mm});
            skLineSegment(sketch, "E109", {"start": v(1.75, -23.3) * mm, "end": v(3.8, -22.67) * mm});
            skLineSegment(sketch, "E110", {"start": v(3.8, -22.67) * mm, "end": v(1.8, -27.43) * mm});
            skLineSegment(sketch, "E111", {"start": v(7.05, -16.28) * mm, "end": v(6.83, -19.35) * mm});
            skLineSegment(sketch, "E112", {"start": v(6.83, -19.35) * mm, "end": v(7.9, -18.78) * mm});
            skLineSegment(sketch, "E113", {"start": v(7.9, -18.78) * mm, "end": v(6.5, -24.9) * mm});
            skFitSpline(sketch, "E114", {"points": [v(7.05, -16.28) * mm, v(6.4, -17.85) * mm, v(5.64, -19.54) * mm, v(5.02, -20.58) * mm, v(4.34, -21.21) * mm, v(4.2, -21.83) * mm], "startDerivative": vector(-2.55, -6.5) * mm, "endDerivative": vector(-0.26, -4.49) * mm});
            skFitSpline(sketch, "E115", {"points": [v(4.2, -21.83) * mm, v(5.06, -21.83) * mm, v(5.84, -22.02) * mm, v(6.37, -22.72) * mm, v(6.5, -24.9) * mm], "startDerivative": vector(3.96, 0.13) * mm, "endDerivative": vector(-0.18, -7.08) * mm});
            skFitSpline(sketch, "E116", {"points": [v(8.73, -13.03) * mm, v(8, -16.1) * mm, v(7.49, -17.24) * mm, v(7.21, -18.26) * mm], "startDerivative": vector(-1.48, -7.58) * mm, "endDerivative": vector(-0.9, -3.78) * mm});
            skFitSpline(sketch, "E117", {"points": [v(7.21, -18.26) * mm, v(7.86, -17.9) * mm, v(8.16, -17.5) * mm, v(8.56, -17.3) * mm], "startDerivative": vector(1.93, 0.78) * mm, "endDerivative": vector(1.47, 0.5) * mm});
            skLineSegment(sketch, "E118", {"start": v(8.73, -13.03) * mm, "end": v(8.87, -14.69) * mm});
            skLineSegment(sketch, "E119", {"start": v(8.87, -14.69) * mm, "end": v(9.96, -13.7) * mm});
            skLineSegment(sketch, "E120", {"start": v(9.96, -13.7) * mm, "end": v(9.48, -20.16) * mm});
            skLineSegment(sketch, "E121", {"start": v(9.48, -20.16) * mm, "end": v(8.56, -17.3) * mm});
            skLineSegment(sketch, "E122", {"start": v(2.6, 11.9) * mm, "end": v(8.25, 9.15) * mm});
            skLineSegment(sketch, "E123", {"start": v(8.25, 9.15) * mm, "end": v(7.78, 8.8) * mm});
            skLineSegment(sketch, "E124", {"start": v(7.78, 8.8) * mm, "end": v(7.34, 9.01) * mm});
            skLineSegment(sketch, "E125", {"start": v(7.34, 9.01) * mm, "end": v(5.42, 8.85) * mm});
            skLineSegment(sketch, "E126", {"start": v(5.42, 8.85) * mm, "end": v(4.86, 6.7) * mm});
            skLineSegment(sketch, "E127", {"start": v(4.86, 6.7) * mm, "end": v(-0.01, 11.05) * mm});
            skLineSegment(sketch, "E128", {"start": v(-0.01, 11.05) * mm, "end": v(2.6, 10.22) * mm});
            skLineSegment(sketch, "E129", {"start": v(2.6, 10.22) * mm, "end": v(2.6, 11.9) * mm});
            skLineSegment(sketch, "E130", {"start": v(-1.39, 14.82) * mm, "end": v(-1.19, 15.79) * mm});
            skLineSegment(sketch, "E131", {"start": v(-1.19, 15.79) * mm, "end": v(5.25, 12.76) * mm});
            skLineSegment(sketch, "E132", {"start": v(1.88, 11.4) * mm, "end": v(2.74, 13.23) * mm});
            skFitSpline(sketch, "E133", {"points": [v(2.74, 13.23) * mm, v(3.3, 13.23) * mm, v(4.3, 12.99) * mm, v(5.25, 12.76) * mm], "startDerivative": vector(1.89, 0.15) * mm, "endDerivative": vector(2.55, -0.57) * mm});
            skFitSpline(sketch, "E134", {"points": [v(-4.36, 15.07) * mm, v(-3.12, 14.65) * mm, v(-2.28, 14.52) * mm, v(-1.66, 14.65) * mm, v(-1.39, 14.82) * mm], "startDerivative": vector(3.87, -1.43) * mm, "endDerivative": vector(1.43, 1.12) * mm});
            skFitSpline(sketch, "E135", {"points": [v(-4.36, 15.07) * mm, v(-0.72, 13.2) * mm, v(0, 12.6) * mm, v(1.14, 11.65) * mm, v(1.88, 11.4) * mm], "startDerivative": vector(11.18, -5.31) * mm, "endDerivative": vector(4.04, -0.78) * mm});
            skLineSegment(sketch, "E136", {"start": v(-9.12, 17.05) * mm, "end": v(-5.88, 17.05) * mm});
            skLineSegment(sketch, "E137", {"start": v(-5.88, 17.05) * mm, "end": v(-5.96, 18.32) * mm});
            skLineSegment(sketch, "E138", {"start": v(-5.96, 18.32) * mm, "end": v(-0.3, 17.65) * mm});
            skLineSegment(sketch, "E139", {"start": v(-0.3, 17.65) * mm, "end": v(-2.86, 16.78) * mm});
            skLineSegment(sketch, "E140", {"start": v(-2.86, 16.78) * mm, "end": v(-2.56, 15.4) * mm});
            skLineSegment(sketch, "E141", {"start": v(-2.56, 15.4) * mm, "end": v(-9.12, 17.05) * mm});
            skLineSegment(sketch, "E142", {"start": v(-11.89, 17.75) * mm, "end": v(-10.3, 19.05) * mm});
            skLineSegment(sketch, "E143", {"start": v(-10.3, 19.05) * mm, "end": v(-11.12, 19.46) * mm});
            skLineSegment(sketch, "E144", {"start": v(-11.12, 19.46) * mm, "end": v(-4.59, 20.3) * mm});
            skLineSegment(sketch, "E145", {"start": v(-7.43, 19.07) * mm, "end": v(-6.75, 17.96) * mm});
            skFitSpline(sketch, "E146", {"points": [v(-11.89, 17.75) * mm, v(-11.07, 17.94) * mm, v(-9.8, 18.04) * mm, v(-6.75, 17.96) * mm], "startDerivative": vector(3.73, 0.83) * mm, "endDerivative": vector(7.45, -0.28) * mm});
            skFitSpline(sketch, "E147", {"points": [v(-7.43, 19.07) * mm, v(-6.75, 19.48) * mm, v(-5.86, 19.82) * mm, v(-4.97, 19.94) * mm, v(-4.59, 20.3) * mm], "startDerivative": vector(2.58, 1.65) * mm, "endDerivative": vector(1.58, 1.99) * mm});
            skFitSpline(sketch, "E148", {"points": [v(-12.5, 19.75) * mm, v(-12.34, 19.07) * mm, v(-12.32, 18.7) * mm, v(-12.68, 18.49) * mm, v(-16.72, 17.75) * mm], "startDerivative": vector(0.84, -3.5) * mm, "endDerivative": vector(-10.31, -1.7) * mm});
            skFitSpline(sketch, "E149", {"points": [v(-12.5, 19.75) * mm, v(-11.89, 20.3) * mm, v(-10.76, 20.75) * mm, v(-10.3, 21.45) * mm], "startDerivative": vector(1.14, 2.05) * mm, "endDerivative": vector(0.92, 2.54) * mm});
            skFitSpline(sketch, "E150", {"points": [v(-16.72, 17.75) * mm, v(-15.3, 18.7) * mm], "startDerivative": vector(1.42, 0.94) * mm, "endDerivative": vector(1.42, 0.94) * mm});
            skFitSpline(sketch, "E151", {"points": [v(-15.3, 18.7) * mm, v(-15.55, 18.87) * mm, v(-15.62, 19.07) * mm, v(-15.3, 19.52) * mm, v(-10.3, 21.45) * mm], "startDerivative": vector(-2.1, 1.23) * mm, "endDerivative": vector(11.3, 3.7) * mm});
            skFitSpline(sketch, "E152", {"points": [v(-20.6, 17.28) * mm, v(-20.11, 17.71) * mm, v(-19.16, 18.44) * mm, v(-18.7, 18.8) * mm, v(-18.5, 19.1) * mm, v(-18.48, 19.4) * mm, v(-18.4, 19.73) * mm, v(-18.06, 20.13) * mm, v(-13.63, 21.97) * mm], "startDerivative": vector(3.83, 3.55) * mm, "endDerivative": vector(18.93, 6.99) * mm});
            skFitSpline(sketch, "E153", {"points": [v(-20.6, 17.28) * mm, v(-19.7, 17.55) * mm, v(-18.95, 17.92) * mm, v(-18.25, 18.25) * mm, v(-17.4, 18.32) * mm, v(-16.94, 18.95) * mm, v(-16.33, 19.9) * mm, v(-15.4, 20.67) * mm, v(-14.47, 21.23) * mm, v(-13.63, 21.97) * mm], "startDerivative": vector(8.47, 2.29) * mm, "endDerivative": vector(6.79, 6.64) * mm});
            skFitSpline(sketch, "E154", {"points": [v(-23.65, 15.71) * mm, v(-22.64, 16.38) * mm, v(-22.01, 17) * mm, v(-21.06, 17.6) * mm, v(-20.73, 17.82) * mm, v(-20.63, 18.25) * mm, v(-20.6, 18.69) * mm, v(-20.53, 19.21) * mm, v(-20.24, 19.91) * mm, v(-19.13, 21.53) * mm, v(-18.13, 22.77) * mm, v(-18.13, 23) * mm], "startDerivative": vector(9.93, 5.79) * mm, "endDerivative": vector(-1.1, 3.95) * mm});
            skFitSpline(sketch, "E155", {"points": [v(-23.65, 15.71) * mm, v(-23.47, 16.24) * mm, v(-22.9, 17.1) * mm, v(-22.5, 17.72) * mm, v(-22.45, 18.29) * mm, v(-22.5, 18.82) * mm, v(-22.22, 19.47) * mm, v(-20.6, 20.96) * mm, v(-18.13, 23) * mm], "startDerivative": vector(1.35, 5.48) * mm, "endDerivative": vector(11.54, 9.48) * mm});
            skFitSpline(sketch, "E156", {"points": [v(-24.1, 17.53) * mm, v(-23.85, 17.9) * mm, v(-23.65, 18.38) * mm, v(-23.77, 18.69) * mm, v(-23.94, 19.16) * mm, v(-23.65, 19.82) * mm, v(-20.6, 23) * mm], "startDerivative": vector(2.09, 2.81) * mm, "endDerivative": vector(10.16, 9.98) * mm});
            skFitSpline(sketch, "E157", {"points": [v(-20.6, 23) * mm, v(-20.93, 22.14) * mm, v(-21.77, 20.87) * mm, v(-22.13, 20.13) * mm, v(-22.1, 19.9) * mm], "startDerivative": vector(-0.92, -3.03) * mm, "endDerivative": vector(0.54, -1.53) * mm});
            skFitSpline(sketch, "E158", {"points": [v(-23.94, 17.05) * mm, v(-23.52, 17.53) * mm, v(-22.87, 18.06) * mm, v(-22.74, 18.4) * mm, v(-22.82, 18.69) * mm, v(-22.84, 19.12) * mm, v(-22.6, 19.47) * mm, v(-22.26, 19.76) * mm, v(-22.1, 19.9) * mm], "startDerivative": vector(2.4, 3.24) * mm, "endDerivative": vector(1.72, 1.46) * mm});
            skFitSpline(sketch, "E159", {"points": [v(6.02, 4.83) * mm, v(6.12, 3.4) * mm, v(6.2, 1.13) * mm, v(5.56, -0.76) * mm, v(4.86, -1.9) * mm], "startDerivative": vector(0.36, -5.88) * mm, "endDerivative": vector(-3.21, -4.88) * mm});
            skFitSpline(sketch, "E160", {"points": [v(6.02, 4.83) * mm, v(7, 3.68) * mm, v(8.04, 1.58) * mm], "startDerivative": vector(2.26, -2.32) * mm, "endDerivative": vector(1.8, -4.1) * mm});
            skFitSpline(sketch, "E161", {"points": [v(8.04, 1.58) * mm, v(8.82, 1.25) * mm, v(10.3, -0.7) * mm, v(12.4, -4.8) * mm], "startDerivative": vector(3.83, -0.97) * mm, "endDerivative": vector(4.57, -9.37) * mm});
            skFitSpline(sketch, "E162", {"points": [v(9.19, -2.53) * mm, v(9.61, -3.43) * mm, v(10.06, -4.03) * mm, v(10.83, -4.35) * mm, v(11.38, -4.38) * mm, v(12.4, -4.8) * mm], "startDerivative": vector(1.93, -4.41) * mm, "endDerivative": vector(4.84, -2.45) * mm});
            skFitSpline(sketch, "E163", {"points": [v(9.19, -2.53) * mm, v(9.33, -3.85) * mm], "startDerivative": vector(0.14, -1.35) * mm, "endDerivative": vector(0.14, -1.35) * mm});
            skFitSpline(sketch, "E164", {"points": [v(9.33, -3.85) * mm, v(10.83, -7.12) * mm, v(11.24, -9.33) * mm], "startDerivative": vector(3.18, -6.09) * mm, "endDerivative": vector(0.55, -4.82) * mm});
            skFitSpline(sketch, "E165", {"points": [v(8.98, -7.9) * mm, v(9.33, -8.5) * mm, v(10.06, -8.75) * mm, v(11.24, -9.33) * mm], "startDerivative": vector(0.93, -2.35) * mm, "endDerivative": vector(3.02, -1.72) * mm});
            skFitSpline(sketch, "E166", {"points": [v(8.98, -7.9) * mm, v(8.98, -8.59) * mm], "startDerivative": vector(0, -0.68) * mm, "endDerivative": vector(0, -0.68) * mm});
            skFitSpline(sketch, "E167", {"points": [v(8.98, -8.59) * mm, v(9.73, -10.21) * mm, v(10.37, -12.04) * mm, v(10.52, -13.18) * mm], "startDerivative": vector(2.12, -4.45) * mm, "endDerivative": vector(0.29, -3.78) * mm});
            skFitSpline(sketch, "E168", {"points": [v(8.44, -10.55) * mm, v(8.62, -11.63) * mm, v(8.98, -12.46) * mm, v(10.06, -12.87) * mm, v(10.52, -13.18) * mm], "startDerivative": vector(0.63, -3.99) * mm, "endDerivative": vector(1.91, -1.71) * mm});
            skFitSpline(sketch, "E169", {"points": [v(8.44, -10.55) * mm, v(8.04, -12.21) * mm, v(7.21, -14.19) * mm, v(6.43, -15.89) * mm, v(5.64, -17.36) * mm, v(4.55, -19.12) * mm, v(2.96, -21.34) * mm, v(1.56, -23.03) * mm, v(0, -24.36) * mm, v(-1.62, -25.46) * mm, v(-5.07, -27.17) * mm, v(-9.13, -28.2) * mm], "startDerivative": vector(-3.94, -21.03) * mm, "endDerivative": vector(-33.6, -6.7) * mm});
            skFitSpline(sketch, "E170", {"points": [v(-9.13, -28.2) * mm, v(-6.61, -27.65) * mm], "startDerivative": vector(2.52, 0.57) * mm, "endDerivative": vector(2.52, 0.57) * mm});
            skFitSpline(sketch, "E171", {"points": [v(-9.13, -28.2) * mm, v(-6.22, -27.12) * mm, v(-4.54, -26.2) * mm, v(-2.48, -24.77) * mm, v(-0.88, -23.44) * mm, v(1.09, -21.44) * mm, v(2.71, -19.3) * mm, v(4.57, -16.26) * mm, v(6.06, -12.87) * mm, v(6.8, -9.1) * mm, v(6.9, -6.05) * mm, v(6.43, -3.97) * mm, v(5.73, -2.53) * mm, v(4.86, -1.9) * mm], "startDerivative": vector(37.26, 12.82) * mm, "endDerivative": vector(-18.85, 9.55) * mm});
            skFitSpline(sketch, "E172", {"points": [v(10.14, 1.25) * mm, v(10.42, 2.08) * mm, v(10.79, 3.05) * mm, v(11.24, 3.85) * mm, v(11.88, 4.4) * mm, v(12.48, 4.56) * mm, v(13.18, 4.14) * mm, v(14.3, 2.97) * mm, v(15.48, 0.94) * mm, v(16.44, -1.04) * mm, v(21.45, -15.15) * mm], "startDerivative": vector(3.72, 13.19) * mm, "endDerivative": vector(21.22, -62.14) * mm});
            skFitSpline(sketch, "E173", {"points": [v(10.14, 1.25) * mm, v(10.57, 1.64) * mm, v(11, 2.02) * mm, v(11.67, 2.22) * mm, v(12.4, 2.1) * mm, v(13.56, 1.25) * mm, v(14.54, 0) * mm, v(16.13, -2.8) * mm, v(21.45, -15.15) * mm], "startDerivative": vector(5.87, 7.31) * mm, "endDerivative": vector(18.33, -44.02) * mm});
            skFitSpline(sketch, "E174", {"points": [v(-29.88, -21.9) * mm, v(-28.22, -23.47) * mm, v(-25.88, -25.01) * mm, v(-23.5, -26.31) * mm, v(-20.71, -27.5) * mm, v(-18.28, -28.25) * mm, v(-15.89, -28.7) * mm, v(-13.73, -28.88) * mm, v(-11.5, -28.65) * mm, v(-9.1, -27.27) * mm], "startDerivative": vector(14.67, -15.22) * mm, "endDerivative": vector(20.39, 14.49) * mm});
            skFitSpline(sketch, "E175", {"points": [v(-29.88, -21.9) * mm, v(-28.72, -22.51) * mm, v(-27.6, -23.44) * mm, v(-26.26, -24.29) * mm, v(-25.17, -24.9) * mm, v(-23.7, -25.6) * mm, v(-21.4, -26.38) * mm, v(-19.64, -26.79) * mm, v(-18.14, -27.06) * mm, v(-16.18, -27.08) * mm, v(-14.52, -26.97) * mm, v(-11.86, -27.27) * mm, v(-9.1, -27.27) * mm], "startDerivative": vector(16.9, -7.57) * mm, "endDerivative": vector(26.4, 1.16) * mm});
            skFitSpline(sketch, "E176", {"points": [v(-35.2, -11.32) * mm, v(-34.48, -13.26) * mm, v(-33.41, -15.32) * mm, v(-32.06, -17.44) * mm, v(-29.88, -19.76) * mm, v(-27.68, -21.61) * mm, v(-24.25, -23.82) * mm, v(-18.05, -26.41) * mm], "startDerivative": vector(5.65, -17.02) * mm, "endDerivative": vector(32.42, -12.23) * mm});
            skFitSpline(sketch, "E177", {"points": [v(-35.2, -11.32) * mm, v(-34.57, -14.07) * mm, v(-33.85, -16.27) * mm, v(-32.66, -18.75) * mm, v(-30.5, -20.71) * mm, v(-29.4, -21.72) * mm, v(-27.26, -23.04) * mm, v(-24.46, -24.44) * mm, v(-20.28, -25.85) * mm, v(-18.05, -26.41) * mm], "startDerivative": vector(5.27, -25.12) * mm, "endDerivative": vector(19.69, -4.62) * mm});
            skFitSpline(sketch, "E178", {"points": [v(-12.05, -23.98) * mm, v(-2.95, -19.87) * mm], "startDerivative": vector(9.1, 4.12) * mm, "endDerivative": vector(9.1, 4.12) * mm});
            skFitSpline(sketch, "E179", {"points": [v(-12.05, -23.98) * mm, v(-10.45, -24.02) * mm, v(-8.74, -23.98) * mm, v(-6.5, -23.38) * mm, v(-3.96, -22.44) * mm], "startDerivative": vector(7.27, -0.1) * mm, "endDerivative": vector(8.92, 3.38) * mm});
            skFitSpline(sketch, "E180", {"points": [v(-2.95, -19.87) * mm, v(-3.8, -19.58) * mm, v(-5.2, -19.22) * mm, v(-6.6, -19.18) * mm, v(-7.95, -19.54) * mm, v(-9.37, -20.39) * mm, v(-10.1, -20.82) * mm, v(-11.4, -21.44) * mm, v(-12.45, -21.8) * mm, v(-14.19, -22.2) * mm, v(-15.9, -22.35) * mm, v(-16.97, -22.38) * mm, v(-18.78, -22.31) * mm, v(-20.73, -21.93) * mm, v(-22.3, -21.44) * mm, v(-23.64, -20.9) * mm, v(-25.54, -19.87) * mm, v(-26.57, -19.1) * mm, v(-27.72, -18.12) * mm, v(-29.1, -16.8) * mm, v(-30.33, -15.34) * mm, v(-30.99, -14.36) * mm, v(-32.05, -12.56) * mm, v(-32.6, -11.32) * mm, v(-33.02, -10.29) * mm, v(-33.41, -8.9) * mm, v(-33.45, -7.47) * mm, v(-33.41, -5.81) * mm, v(-33.12, -4.05) * mm, v(-32.44, -2.3) * mm, v(-31.62, -0.7) * mm, v(-30.5, 0.74) * mm, v(-29.44, 1.77) * mm, v(-28.22, 2.54) * mm, v(-26.09, 3.04) * mm, v(-23.88, 3.39) * mm], "startDerivative": vector(-36.32, 12.77) * mm, "endDerivative": vector(63.9, 10.04) * mm});
            skFitSpline(sketch, "E181", {"points": [v(-33.32, 0.72) * mm, v(-32.75, 1.39) * mm, v(-31.65, 2.22) * mm, v(-30.24, 3.02) * mm, v(-28.64, 3.42) * mm, v(-25.83, 3.66) * mm, v(-23.88, 3.39) * mm], "startDerivative": vector(4.3, 5.78) * mm, "endDerivative": vector(10.03, -1.95) * mm});
            skFitSpline(sketch, "E182", {"points": [v(-33.32, 0.72) * mm, v(-33.32, 1.39) * mm, v(-32.45, 3.2) * mm], "startDerivative": vector(-0.25, 1.64) * mm, "endDerivative": vector(1.8, 3.17) * mm});
            skFitSpline(sketch, "E183", {"points": [v(-32.45, 3.2) * mm, v(-33.32, 2.82) * mm, v(-34.25, 1.89) * mm, v(-34.85, 0.72) * mm, v(-35.39, -1.09) * mm, v(-35.46, -1.65) * mm], "startDerivative": vector(-4.83, -1.5) * mm, "endDerivative": vector(-0.18, -3.37) * mm});
            skFitSpline(sketch, "E184", {"points": [v(-35.72, 1.95) * mm, v(-35.96, 0.72) * mm, v(-35.79, -0.55) * mm, v(-35.46, -1.65) * mm], "startDerivative": vector(-0.97, -3.63) * mm, "endDerivative": vector(1.1, -3.33) * mm});
            skFitSpline(sketch, "E185", {"points": [v(-35.72, 1.95) * mm, v(-36.35, 0.72) * mm, v(-36.72, -1.09) * mm, v(-36.6, -3.5) * mm, v(-36.32, -5.46) * mm, v(-35.95, -7.4) * mm], "startDerivative": vector(-4, -6.88) * mm, "endDerivative": vector(1.92, -9.63) * mm});
            skFitSpline(sketch, "E186", {"points": [v(-35.95, -7.4) * mm, v(-36.76, -6.4) * mm, v(-37.23, -5.3) * mm, v(-37.54, -4.05) * mm, v(-37.8, -2.64) * mm], "startDerivative": vector(-3.58, 3.87) * mm, "endDerivative": vector(-1.02, 5.44) * mm});
            skFitSpline(sketch, "E187", {"points": [v(-37.8, -2.64) * mm, v(-37.8, -4.86) * mm, v(-37.27, -7.4) * mm, v(-35.95, -9.64) * mm, v(-35.2, -10.54) * mm], "startDerivative": vector(-0.3, -8.5) * mm, "endDerivative": vector(3.76, -4.21) * mm});
            skFitSpline(sketch, "E188", {"points": [v(-35.2, -10.54) * mm, v(-35.46, -9.43) * mm, v(-35.6, -7.32) * mm, v(-35.52, -6.18) * mm, v(-35.2, -4.1) * mm, v(-34.46, -2.08) * mm, v(-33.32, -0.4) * mm, v(-32.15, 0.72) * mm, v(-31.08, 1.52) * mm, v(-30.54, 1.74) * mm], "startDerivative": vector(-3.1, 10.15) * mm, "endDerivative": vector(7.3, 2.34) * mm});
            skFitSpline(sketch, "E189", {"points": [v(-3.96, -22.44) * mm, v(-6.12, -23.73) * mm, v(-7.8, -24.62) * mm, v(-9.44, -25.26) * mm, v(-11.23, -25.68) * mm, v(-13.6, -25.89) * mm, v(-15.55, -25.84) * mm, v(-17.45, -25.57) * mm, v(-19.77, -25.1) * mm, v(-22.08, -24.15) * mm, v(-24.09, -23.2) * mm, v(-25.4, -22.44) * mm, v(-27.51, -20.83) * mm, v(-29.25, -18.98) * mm, v(-30.46, -17.56) * mm, v(-31.36, -16.3) * mm, v(-32.2, -14.98) * mm, v(-32.94, -13.4) * mm, v(-33.57, -11.82) * mm, v(-34, -10.46) * mm, v(-34.3, -9.1) * mm, v(-34.42, -7.13) * mm, v(-34.3, -5.35) * mm, v(-33.77, -3.27) * mm, v(-32.87, -1.24) * mm, v(-32.04, 0) * mm, v(-30.54, 1.74) * mm], "startDerivative": vector(-50.97, -30.73) * mm, "endDerivative": vector(39.16, 43.84) * mm});
            skFitSpline(sketch, "E190", {"points": [v(4.3, 5.74) * mm, v(4.6, 5.37) * mm], "startDerivative": vector(0.29, -0.37) * mm, "endDerivative": vector(0.29, -0.37) * mm});
            skFitSpline(sketch, "E191", {"points": [v(4.6, 5.37) * mm, v(5.17, 5.37) * mm, v(6.2, 5.06) * mm, v(7.17, 4.35) * mm, v(7.78, 3.37) * mm, v(8.2, 2.32) * mm, v(8.62, 1.77) * mm], "startDerivative": vector(4.14, 0.3) * mm, "endDerivative": vector(3.16, -3.4) * mm});
            skFitSpline(sketch, "E192", {"points": [v(8.62, 1.77) * mm, v(10.96, 7.9) * mm, v(11.34, 8.88) * mm, v(11.67, 10.8) * mm, v(11.93, 11.96) * mm, v(12.39, 12.88) * mm, v(13.1, 13.35) * mm, v(14.82, 13.43) * mm], "startDerivative": vector(10.31, 27.62) * mm, "endDerivative": vector(13.58, -0.37) * mm});
            skFitSpline(sketch, "E193", {"points": [v(2.33, 22.82) * mm, v(4.21, 21.76) * mm, v(6.26, 20.45) * mm, v(8.82, 18.6) * mm, v(12.5, 15.67) * mm, v(14.82, 13.43) * mm], "startDerivative": vector(11.18, -6.15) * mm, "endDerivative": vector(10.26, -10.6) * mm});
            skFitSpline(sketch, "E194", {"points": [v(4.3, 5.74) * mm, v(5.44, 6.13) * mm, v(6.5, 6.13) * mm, v(7.28, 6.45) * mm, v(8.62, 7.74) * mm, v(9.36, 8.88) * mm, v(10.07, 10.8) * mm, v(10.07, 12.83) * mm, v(9.32, 15.46) * mm, v(7.87, 17.3) * mm, v(6.19, 18.75) * mm, v(3.8, 20.63) * mm, v(0, 23.06) * mm, v(-2.87, 24.37) * mm, v(-4.54, 24.95) * mm, v(-6.38, 25) * mm], "startDerivative": vector(21.92, 10.03) * mm, "endDerivative": vector(-30, -1.44) * mm});
            skFitSpline(sketch, "E195", {"points": [v(-6.38, 25) * mm, v(-5.42, 25.58) * mm, v(-3.45, 25.96) * mm], "startDerivative": vector(1.99, 1.52) * mm, "endDerivative": vector(3.78, 0.46) * mm});
            skFitSpline(sketch, "E196", {"points": [v(-3.45, 25.96) * mm, v(-5.24, 25.96) * mm, v(-6.95, 25.53) * mm, v(-8.33, 25) * mm, v(-9.2, 24.59) * mm, v(-10.13, 24.04) * mm, v(-11.24, 23.23) * mm], "startDerivative": vector(-9.52, 0.53) * mm, "endDerivative": vector(-6.78, -5.12) * mm});
            skFitSpline(sketch, "E197", {"points": [v(-11.24, 23.23) * mm, v(-10.86, 24.26) * mm, v(-9.57, 25.87) * mm, v(-8.53, 26.78) * mm, v(-6.9, 27.74) * mm, v(-6.03, 27.96) * mm, v(-5.32, 27.96) * mm, v(-4.38, 28.16) * mm, v(-3.17, 28.77) * mm, v(0, 29.6) * mm], "startDerivative": vector(2.4, 10.05) * mm, "endDerivative": vector(21.26, 4.43) * mm});
            skFitSpline(sketch, "E198", {"points": [v(-3.35, 28.69) * mm, v(-2.42, 29.03) * mm, v(-0.66, 29.64) * mm, v(1.06, 30.12) * mm, v(3.15, 30.64) * mm, v(5.67, 31.03) * mm, v(7.32, 31.21) * mm, v(11.2, 31.21) * mm], "startDerivative": vector(8.55, 3.1) * mm, "endDerivative": vector(22.21, -0.4) * mm});
            skFitSpline(sketch, "E199", {"points": [v(6.43, 31.13) * mm, v(7.32, 31.21) * mm, v(10.77, 31.05) * mm, v(12.19, 30.86) * mm, v(13.84, 30.55) * mm, v(16.48, 29.45) * mm, v(19.3, 27.67) * mm, v(24.11, 24.1) * mm, v(27.26, 21.31) * mm, v(28.71, 19.83) * mm, v(30.7, 17.39) * mm, v(32.9, 14.66) * mm, v(36.41, 9.01) * mm, v(37.8, 5.95) * mm], "startDerivative": vector(16.57, 2.6) * mm, "endDerivative": vector(13.94, -34.05) * mm});
            skFitSpline(sketch, "E200", {"points": [v(-0.62, 27.94) * mm, v(1.44, 28.59) * mm, v(4.37, 29.53) * mm, v(6.73, 29.88) * mm, v(9.5, 30.06) * mm, v(12.2, 29.94) * mm, v(16.48, 28.59) * mm, v(20.54, 26.12) * mm, v(24.36, 23.12) * mm, v(27.3, 20.12) * mm, v(29.48, 17.42) * mm, v(32.06, 13.3) * mm, v(33, 10.54) * mm, v(33.24, 9.83) * mm, v(34.12, 9.36) * mm, v(35.35, 8.66) * mm, v(37.8, 5.95) * mm], "startDerivative": vector(36.07, 10.93) * mm, "endDerivative": vector(37.44, -45.6) * mm});
            skFitSpline(sketch, "E201", {"points": [v(-0.62, 27.94) * mm, v(2.28, 27.94) * mm, v(6.33, 27.94) * mm, v(11.05, 27.2) * mm, v(16.07, 25.5) * mm, v(19.53, 23.22) * mm, v(22.4, 20.2) * mm, v(24.92, 16.88) * mm, v(26.76, 13.93) * mm, v(28.38, 11.27) * mm, v(30.52, 6.85) * mm, v(31.92, 2.72) * mm, v(33.18, -1.78) * mm, v(34.13, -5.9) * mm, v(34.13, -10.11) * mm], "startDerivative": vector(46.58, -0.46) * mm, "endDerivative": vector(-3.32, -59.06) * mm});
            skFitSpline(sketch, "E202", {"points": [v(0.02, 25.95) * mm, v(2.5, 26.24) * mm, v(6.63, 26.1) * mm, v(10.17, 25.88) * mm, v(14.15, 24.77) * mm, v(17.03, 23.6) * mm, v(20.05, 21.6) * mm, v(22.19, 19.17) * mm, v(24.92, 15.63) * mm, v(26.98, 11.94) * mm, v(28.68, 8.47) * mm, v(29.93, 5.23) * mm, v(30.96, 0) * mm, v(31.18, -3.84) * mm, v(31.4, -4.8) * mm, v(32.14, -5.54) * mm, v(33.4, -7.9) * mm, v(34.13, -10.11) * mm], "startDerivative": vector(43.97, 7.68) * mm, "endDerivative": vector(12.63, -42.2) * mm});
            skFitSpline(sketch, "E203", {"points": [v(0.02, 25.95) * mm, v(1.15, 25.55) * mm, v(2.28, 24.8) * mm, v(3.92, 24.27) * mm, v(6.28, 23.51) * mm, v(9, 22.31) * mm, v(11.96, 20.75) * mm, v(14.4, 19.19) * mm, v(17.8, 16.27) * mm, v(20.2, 13.02) * mm, v(22.4, 8.08) * mm, v(23.76, 2.49) * mm, v(24.92, -3.82) * mm, v(25.38, -12.34) * mm, v(23.29, -22.68) * mm], "startDerivative": vector(29.77, -7.5) * mm, "endDerivative": vector(-23.7, -90.27) * mm});
            skFitSpline(sketch, "E204", {"points": [v(2.33, 22.82) * mm, v(6.28, 21.7) * mm, v(10, 20.2) * mm, v(14.42, 17.57) * mm, v(18.2, 14.41) * mm, v(20.39, 9.85) * mm, v(22.4, 3.42) * mm, v(23.29, -3.99) * mm, v(23.29, -12.34) * mm, v(22.4, -16.08) * mm, v(21.45, -17.1) * mm, v(22.4, -19.19) * mm, v(23.29, -22.68) * mm], "startDerivative": vector(50.55, -13.66) * mm, "endDerivative": vector(7.17, -49.05) * mm});
            skSolve(sketch);
        }
        {
            var Q0;
            Q0 = qSketchRegion(id + "F10", true);
            extrude(context, id + "F11", {"entities" : qUnion([Q0]), "operationType" : NewBodyOperationType.REMOVE, "oppositeDirection" : true, "depth" : 0.64 * mm, "offsetDistance" : 25.4 * mm});
        }
        {
            var Q0;
            {var subQ0=sQuery(id+"F0.wireOp",EDGE,"E0");Q0=makeQuery(id+"F11.boolean.opBoolean","SPLIT",FACE,{"disambiguationData":[TD([makeQuery(id+"F11.opExtrude","SWEPT_FACE",FACE,{"disambiguationData":[OSD([sQuery(id+"F10.wireOp",EDGE,"E4")])]})])],"derivedFrom":makeQuery(id+"F1.opExtrude","CAP_FACE",FACE,{"disambiguationData":[OSD([subQ0])],"isStart":false})});}
            var sketch = newSketch(context, id + "F12", { "sketchPlane" : qUnion([Q0])});
            skFitSpline(sketch, "E205", {"points": [v(8.5, 2.1) * mm, v(10.14, 1.25) * mm], "startDerivative": vector(1.64, -0.85) * mm, "endDerivative": vector(1.64, -0.85) * mm});
            skFitSpline(sketch, "E206", {"points": [v(8.5, 2.1) * mm, v(9.56, 6.98) * mm, v(11.4, 14.53) * mm, v(8.04, 18.34) * mm, v(2.33, 22.82) * mm], "startDerivative": vector(2.88, 19.78) * mm, "endDerivative": vector(-21.42, 17.33) * mm});
            skFitSpline(sketch, "E207", {"points": [v(23.29, -18.14) * mm, v(21.45, -15.15) * mm], "startDerivative": vector(-1.84, 3) * mm, "endDerivative": vector(-1.84, 3) * mm});
            skFitSpline(sketch, "E208", {"points": [v(21.45, -15.15) * mm, v(16.78, -1.88) * mm], "startDerivative": vector(-4.69, 13.26) * mm, "endDerivative": vector(-4.69, 13.26) * mm});
            skFitSpline(sketch, "E209", {"points": [v(16.78, -1.88) * mm, v(12.57, 2.97) * mm, v(10.14, 1.25) * mm], "startDerivative": vector(-7.38, 11.82) * mm, "endDerivative": vector(-5.8, -6.73) * mm});
            skFitSpline(sketch, "E210", {"points": [v(23.29, -18.14) * mm, v(22.76, 1.58) * mm, v(19, 14.87) * mm, v(5.6, 22.82) * mm, v(2.33, 22.82) * mm], "startDerivative": vector(-1.15, 64.35) * mm, "endDerivative": vector(-19.9, -3.97) * mm});
            skFitSpline(sketch, "E211", {"points": [v(23.29, -18.14) * mm, v(24.25, -6.2) * mm, v(22.76, 1.58) * mm], "startDerivative": vector(3.14, 22.85) * mm, "endDerivative": vector(-4.45, 16.38) * mm});
            skFitSpline(sketch, "E212", {"points": [v(22.39, 6.53) * mm, v(19.03, 14.17) * mm, v(15.91, 17.72) * mm], "startDerivative": vector(-5.45, 14.86) * mm, "endDerivative": vector(-7.6, 7.13) * mm});
            skFitSpline(sketch, "E213.trimOffspring", {"points": [v(23.29, -18.14) * mm, v(22.76, 1.58) * mm, v(19, 14.87) * mm, v(5.6, 22.82) * mm, v(2.33, 22.82) * mm], "startDerivative": vector(-1.15, 64.35) * mm, "endDerivative": vector(-19.9, -3.97) * mm});
            skFitSpline(sketch, "E214", {"points": [v(23.29, -22.68) * mm, v(31.22, -4.27) * mm], "startDerivative": vector(7.94, 18.41) * mm, "endDerivative": vector(7.94, 18.41) * mm});
            skFitSpline(sketch, "E215", {"points": [v(23.29, -18.14) * mm, v(23.29, -22.68) * mm], "startDerivative": vector(0, -4.54) * mm, "endDerivative": vector(0, -4.54) * mm});
            skFitSpline(sketch, "E216", {"points": [v(25.93, -16.55) * mm, v(30.09, -10.11) * mm, v(33.32, -7.71) * mm], "startDerivative": vector(7.01, 12.66) * mm, "endDerivative": vector(7.79, 4.57) * mm});
            skFitSpline(sketch, "E217", {"points": [v(3.2, 23) * mm, v(-1.81, 25.96) * mm, v(3.2, 27.15) * mm], "startDerivative": vector(-14.87, 6.6) * mm, "endDerivative": vector(15.17, 1.67) * mm});
            skFitSpline(sketch, "E218", {"points": [v(3.2, 27.15) * mm, v(11.15, 26.55) * mm, v(18.96, 23) * mm, v(24.04, 17.56) * mm, v(27.1, 12.58) * mm, v(28.93, 8.93) * mm, v(32.35, -2.36) * mm, v(31.22, -4.27) * mm], "startDerivative": vector(50.09, 0) * mm, "endDerivative": vector(-18.98, -15.22) * mm});
            skFitSpline(sketch, "E219", {"points": [v(31.22, -4.27) * mm, v(33.22, -4.97) * mm, v(33.32, -7.71) * mm], "startDerivative": vector(5.22, -0.64) * mm, "endDerivative": vector(-0.9, -6.12) * mm});
            skFitSpline(sketch, "E220", {"points": [v(34.13, -10.11) * mm, v(34.13, 1.89) * mm, v(36.92, 7.03) * mm], "startDerivative": vector(-2, 22.7) * mm, "endDerivative": vector(8.15, 10.89) * mm});
            skFitSpline(sketch, "E221", {"points": [v(33.48, -6.62) * mm, v(34.13, -10.11) * mm], "startDerivative": vector(0.65, -3.49) * mm, "endDerivative": vector(0.65, -3.49) * mm});
            skFitSpline(sketch, "E222", {"points": [v(-1.81, 25.96) * mm, v(-2.02, 27.94) * mm, v(6.8, 30.6) * mm, v(15.08, 29.67) * mm, v(26.59, 21.48) * mm, v(34.13, 10.46) * mm], "startDerivative": vector(-10.14, 21.51) * mm, "endDerivative": vector(25.97, -45.84) * mm});
            skFitSpline(sketch, "E223", {"points": [v(34.13, 10.46) * mm, v(36.92, 7.03) * mm], "startDerivative": vector(2.78, -3.43) * mm, "endDerivative": vector(2.78, -3.43) * mm});
            skSolve(sketch);
        }
        {
            var Q0;
            Q0 = qSketchRegion(id + "F12", true);
            var Q1;
            Q1=makeQuery(id+"F12.imprint","IMPRINT",FACE,{"disambiguationData":[TD([[makeQuery(id+"F12.imprint","IMPRINT",EDGE,{"derivedFrom":sQuery(id+"F12.wireOp",EDGE,"E214")}),1.0]])]});
            var Q2;
            {var subQ1=makeQuery(id+"F11.boolean.opBoolean","COPY",EDGE,{"derivedFrom":makeQuery(id+"F11.opExtrude","CAP_EDGE",EDGE,{"disambiguationData":[OSD([sQuery(id+"F10.wireOp",EDGE,"E200")])],"isStart":true})});var subQ3=makeQuery(id+"F11.boolean.opBoolean","COPY",EDGE,{"derivedFrom":makeQuery(id+"F11.opExtrude","CAP_EDGE",EDGE,{"disambiguationData":[OSD([sQuery(id+"F10.wireOp",EDGE,"E201")])],"isStart":true})});var subQ5=makeQuery(id+"F12.imprint","INTERSECT",VERTEX,{"derivedFrom":[subQ1,subQ3]});Q2=makeQuery(id+"F12.imprint","IMPRINT",FACE,{"disambiguationData":[TD([[makeQuery(id+"F12.imprint","IMPRINT",EDGE,{"disambiguationData":[TD([[subQ5,-1.0]])],"derivedFrom":subQ3}),1.0]])]});}
            extrude(context, id + "F13", {"entities" : qUnion([Q0, Q1, Q2]), "operationType" : NewBodyOperationType.REMOVE, "oppositeDirection" : true, "depth" : 0.25 * mm, "offsetDistance" : 25.4 * mm});
        }
    });
